# Revit family: LSRK
name_source: partatom
category: Lighting Fixtures
units: mm (PartAtom-declared; Revit-internal decimal feet)

## family parameters
Cut with Voids When Loaded = No
Host = Face
Light Source = Yes
OmniClass Number = 23.80.70.11
OmniClass Title = Luminaries for Internal Lighting
Part Type = Normal
Room Calculation Point = No
Round Connector Dimension = Use Diameter
Shared = No

## types (1)
- LSRK-5W-35LW-FA-EDU
    Apparent Load = 5 VA
    Color Filter = 16777215
    Default Elevation = 48"
    Description = Linear Strip Retrofit Kit / LED
    Dimming Lamp Color Temperature Shift = Incandescent Lamp Curve
    Emit Shape Visible in Rendering = No
    Emit from Rectangle Length = 47"
    Emit from Rectangle Width = 2 1/2"
    Finish = White
    Glass = White Glass
    Lamp = LED
    Load Classification = Lighting
    Lumen Output = Low Watt
    Manufacturer = Columbia Lighting
    Model = LSRK
    Mounting = Wall Mount
    Photometric Notes = More IES files download Photometric Web Link
    Photometric Web File = generic.ies
    Power Factor = 1
    Shielding = Frosted Acrylic Lens with Endcaps
    Tilt Angle = 90.00°
    URL = https://www.currentlighting.com
    Voltage = 120 V
    Warranty = Five year warranty
    Wattage Comments = Replaces outdated, non-efficient strip lighting with low wattage, high lumen solutions
    Watts = 5 W

## geometry (parser evidence)
native form markers: Blend x6, Sweep x3
no freeform markers — native parametric forms only
